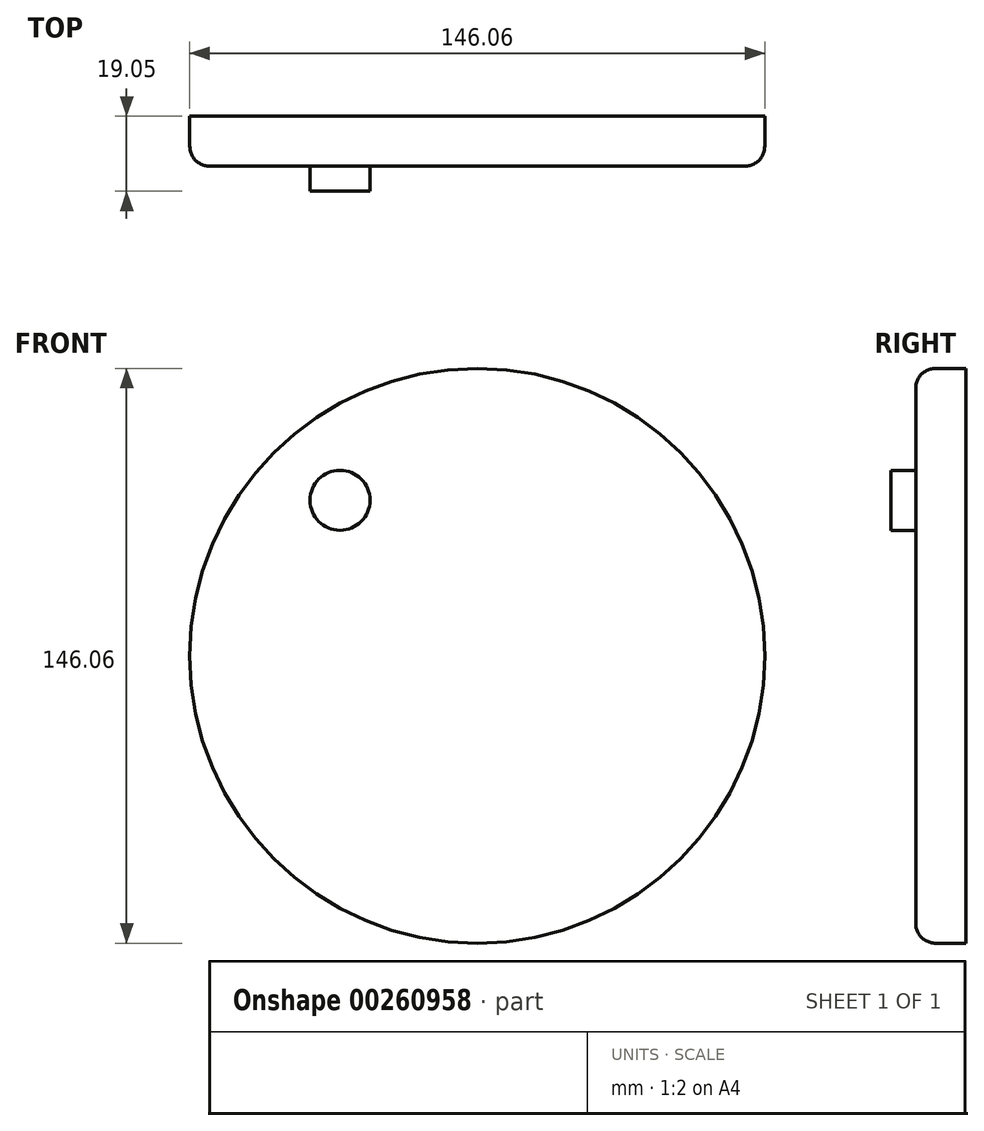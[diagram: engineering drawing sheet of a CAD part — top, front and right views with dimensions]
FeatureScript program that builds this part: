
annotation { "Feature Type Name" : "Feature", "Feature Type Description" : "" }
export const myFeature = defineFeature(function(context is Context, id is Id, definition is map)
    precondition{}
    {
        {
            var Q0;
            Q0=qCreatedBy(makeId("Front.planeOp"),FACE);
            var sketch = newSketch(context, id + "F0", { "sketchPlane" : qUnion([Q0])});
            skCircle(sketch, "E0", {"center": v(0, 0) * mm, "radius": 73.02 * mm});
            skPoint(sketch, "E1", {"position": v(-34.88, 39.52) * mm});
            skCircle(sketch, "E2", {"center": v(-34.88, 39.52) * mm, "radius": 7.62 * mm});
            skSolve(sketch);
        }
        {
            var Q0;
            Q0 = qSketchRegion(id + "F0", true);
            extrude(context, id + "F1", {"entities" : qUnion([Q0]), "depth" : 12.7 * mm});
        }
        {
            var Q0;
            Q0=makeQuery(id+"F1.opExtrude","CAP_EDGE",EDGE,{"disambiguationData":[OSD([sQuery(id+"F0.wireOp",EDGE,"E0")])],"isStart":false});
            fillet(context, id + "F2", {"entities" : qUnion([Q0]), "radius" : 5.08 * mm, "tangentPropagation" : true, "allowEdgeOverflow" : false});
        }
        {
            var Q0;
            Q0=makeQuery(id+"F0.imprint","IMPRINT",FACE,{"disambiguationData":[TD([[makeQuery(id+"F0.imprint","IMPRINT",EDGE,{"derivedFrom":sQuery(id+"F0.wireOp",EDGE,"E2")}),1.0]])]});
            extrude(context, id + "F3", {"entities" : qUnion([Q0]), "operationType" : NewBodyOperationType.ADD, "depth" : 19.05 * mm});
        }
    });
